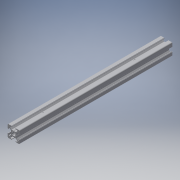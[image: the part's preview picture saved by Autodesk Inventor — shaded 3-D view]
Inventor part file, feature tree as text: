
AUTODESK INVENTOR PART (.ipt)
format: ipt  version: 2017 (Build 210142000, 142)  size: 404,480 bytes
history: native  units: in
note: dims shown in document units (in); Inventor stores cm internally (conversion verified against a paired STEP export)
features: other x3, sketch x2, extrude x1, hole x1, mirror x1
ambient origin geometry x8: Origin, YZ Plane, XZ Plane, XY Plane, X Axis, Y Axis, Z Axis, Center Point
bodies: Solid1 (feature_tree)
feature tree (8):
  other  "Blocks"
  extrude  "Extrusion1"  Depth=2.0in
  hole  "Hole1"  [1 undecoded]
  mirror  "Mirror1"
  sketch  "Sketch1"  dims[d1=0.0in d5=2.0in]
  other  "20x20"
  sketch  "Sketch3"  dims[d6=0.187in d7=0.75in d8=0.375in d9=0.25in d10=0.5635in d11=1.0in d12=0.8108in d13=1.0in d14=1.0in]
  other  "20x20:1"
note: 1 required parameter value undecoded (feature->parameter linkage not recoverable at this tier; creation-order binding heuristic only, values carry confidence <= 0.55)
